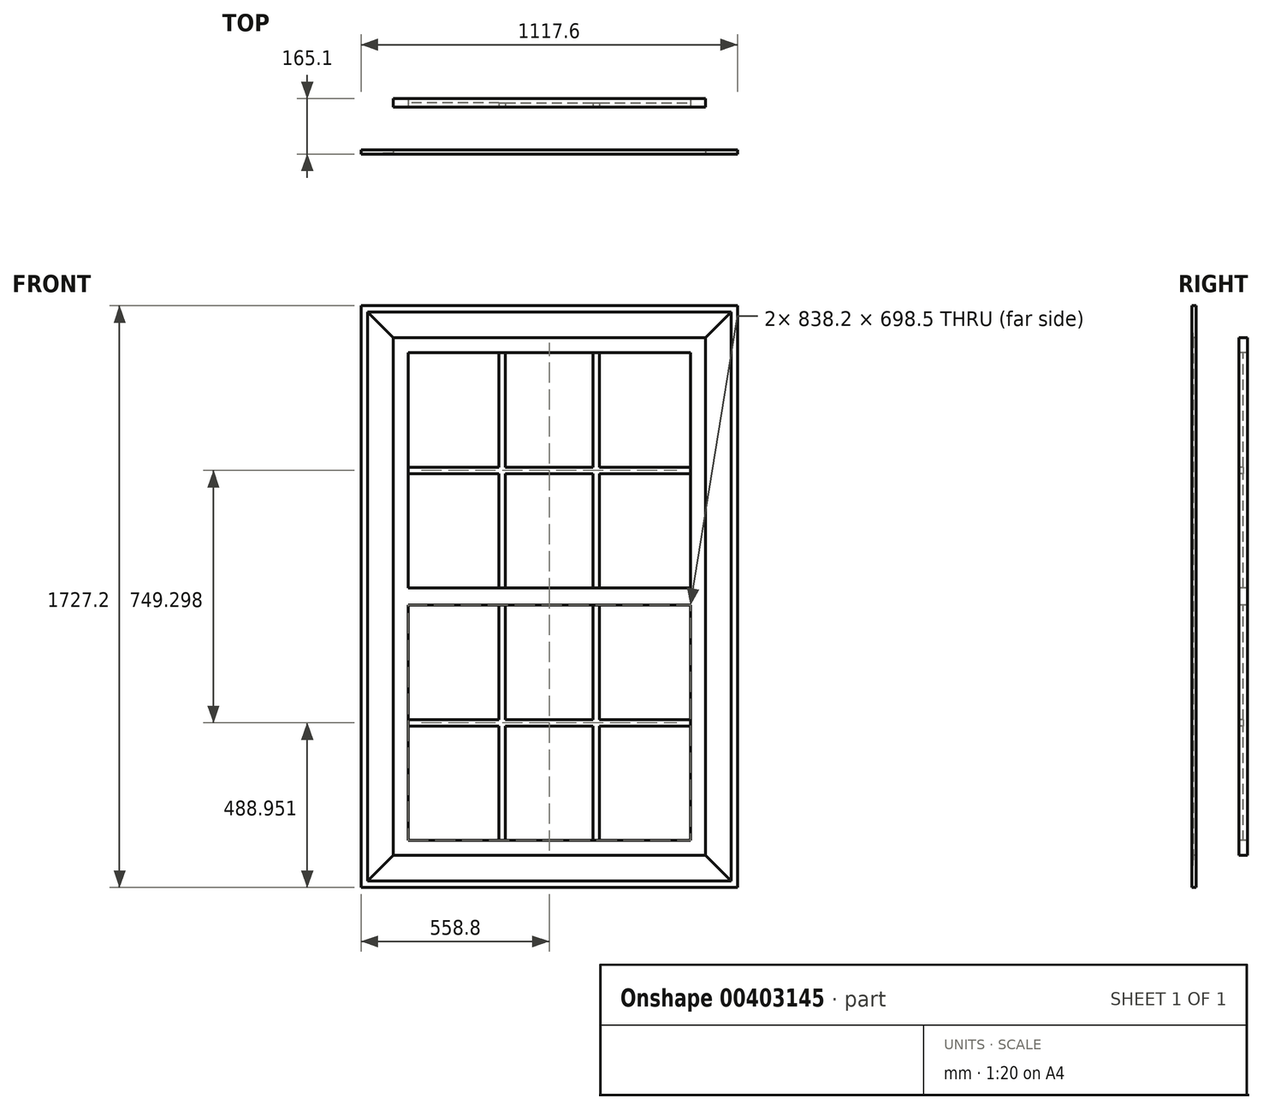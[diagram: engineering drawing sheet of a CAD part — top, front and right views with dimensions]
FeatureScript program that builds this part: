
annotation { "Feature Type Name" : "Feature", "Feature Type Description" : "" }
export const myFeature = defineFeature(function(context is Context, id is Id, definition is map)
    precondition{}
    {
        {
            var Q0;
            Q0=qCreatedBy(makeId("Front.planeOp"),FACE);
            var sketch = newSketch(context, id + "F0", { "sketchPlane" : qUnion([Q0])});
            skLineSegment(sketch, "E0.bottom", {"start": v(463.55, 768.35) * mm, "end": v(-463.55, 768.35) * mm});
            skLineSegment(sketch, "E0.top", {"start": v(463.55, -768.35) * mm, "end": v(-463.55, -768.35) * mm});
            skLineSegment(sketch, "E0.left", {"start": v(463.55, 768.35) * mm, "end": v(463.55, -768.35) * mm});
            skLineSegment(sketch, "E0.right", {"start": v(-463.55, 768.35) * mm, "end": v(-463.55, -768.35) * mm});
            skPoint(sketch, "E0.middle", {"position": v(0, 0) * mm});
            skLineSegment(sketch, "E1.0", {"start": v(-558.8, 863.6) * mm, "end": v(-558.8, -863.6) * mm});
            skLineSegment(sketch, "E1.1", {"start": v(558.8, 863.6) * mm, "end": v(-558.8, 863.6) * mm});
            skLineSegment(sketch, "E1.2", {"start": v(558.8, 863.6) * mm, "end": v(558.8, -863.6) * mm});
            skLineSegment(sketch, "E1.3", {"start": v(558.8, -863.6) * mm, "end": v(-558.8, -863.6) * mm});
            skLineSegment(sketch, "E2.0", {"start": v(-419.1, 723.9) * mm, "end": v(-419.1, -723.9) * mm});
            skLineSegment(sketch, "E2.1", {"start": v(419.1, 723.9) * mm, "end": v(-419.1, 723.9) * mm});
            skLineSegment(sketch, "E2.2", {"start": v(419.1, 723.9) * mm, "end": v(419.1, -723.9) * mm});
            skLineSegment(sketch, "E2.3", {"start": v(419.1, -723.9) * mm, "end": v(-419.1, -723.9) * mm});
            skLineSegment(sketch, "E3", {"start": v(-419.1, 0) * mm, "end": v(419.1, 0) * mm, "construction": true});
            skLineSegment(sketch, "E4.0", {"start": v(-419.1, 25.4) * mm, "end": v(419.1, 25.4) * mm});
            skLineSegment(sketch, "E5", {"start": v(-139.7, 723.9) * mm, "end": v(-139.7, 25.4) * mm, "construction": true});
            skLineSegment(sketch, "E6", {"start": v(139.7, 723.9) * mm, "end": v(139.7, 25.4) * mm, "construction": true});
            skLineSegment(sketch, "E7", {"start": v(-419.1, 374.65) * mm, "end": v(-139.7, 374.65) * mm, "construction": true});
            skLineSegment(sketch, "E8", {"start": v(-139.7, 374.65) * mm, "end": v(139.7, 374.65) * mm, "construction": true});
            skLineSegment(sketch, "E9", {"start": v(139.7, 374.65) * mm, "end": v(419.1, 374.65) * mm, "construction": true});
            skLineSegment(sketch, "E10", {"start": v(-419.1, 365.12) * mm, "end": v(-149.22, 365.12) * mm});
            skLineSegment(sketch, "E11", {"start": v(-149.22, 365.12) * mm, "end": v(-149.22, 25.4) * mm});
            skLineSegment(sketch, "E12", {"start": v(-419.1, 384.17) * mm, "end": v(-149.22, 384.17) * mm});
            skLineSegment(sketch, "E13", {"start": v(-149.22, 384.17) * mm, "end": v(-149.22, 723.9) * mm});
            skLineSegment(sketch, "E14", {"start": v(-130.17, 723.9) * mm, "end": v(-130.17, 384.17) * mm});
            skLineSegment(sketch, "E15", {"start": v(-130.17, 384.17) * mm, "end": v(130.17, 384.17) * mm});
            skLineSegment(sketch, "E16", {"start": v(130.17, 384.17) * mm, "end": v(130.17, 723.9) * mm});
            skLineSegment(sketch, "E17", {"start": v(149.22, 723.9) * mm, "end": v(149.22, 384.17) * mm});
            skLineSegment(sketch, "E18", {"start": v(149.22, 384.17) * mm, "end": v(419.1, 384.17) * mm});
            skLineSegment(sketch, "E19", {"start": v(419.1, 365.12) * mm, "end": v(149.22, 365.12) * mm});
            skLineSegment(sketch, "E20", {"start": v(149.22, 365.12) * mm, "end": v(149.22, 25.4) * mm});
            skLineSegment(sketch, "E21", {"start": v(130.17, 25.4) * mm, "end": v(130.17, 365.12) * mm});
            skLineSegment(sketch, "E22", {"start": v(130.17, 365.12) * mm, "end": v(-130.17, 365.12) * mm});
            skLineSegment(sketch, "E23", {"start": v(-130.17, 365.12) * mm, "end": v(-130.17, 25.4) * mm});
            skLineSegment(sketch, "E24", {"start": v(-149.22, 384.17) * mm, "end": v(-130.17, 365.12) * mm, "construction": true});
            skLineSegment(sketch, "E25", {"start": v(130.17, 384.17) * mm, "end": v(149.22, 365.12) * mm, "construction": true});
            skLineSegment(sketch, "E26.MirrorCS", {"start": v(-149.22, -384.17) * mm, "end": v(-130.17, -365.12) * mm, "construction": true});
            skLineSegment(sketch, "E27.MirrorCS", {"start": v(130.17, -384.17) * mm, "end": v(149.22, -365.12) * mm, "construction": true});
            skLineSegment(sketch, "E28.MirrorCS", {"start": v(-149.22, -365.12) * mm, "end": v(-149.22, -25.4) * mm});
            skLineSegment(sketch, "E29.MirrorCS", {"start": v(-130.17, -365.12) * mm, "end": v(-130.17, -25.4) * mm});
            skLineSegment(sketch, "E30.MirrorCS", {"start": v(-419.1, -365.12) * mm, "end": v(-149.22, -365.12) * mm});
            skLineSegment(sketch, "E31.MirrorCS", {"start": v(-419.1, -384.17) * mm, "end": v(-149.22, -384.17) * mm});
            skLineSegment(sketch, "E32.MirrorCS", {"start": v(-149.22, -384.17) * mm, "end": v(-149.22, -723.9) * mm});
            skLineSegment(sketch, "E33.MirrorCS", {"start": v(-130.17, -723.9) * mm, "end": v(-130.17, -384.17) * mm});
            skLineSegment(sketch, "E34.MirrorCS", {"start": v(-130.17, -384.17) * mm, "end": v(130.17, -384.17) * mm});
            skLineSegment(sketch, "E35.MirrorCS", {"start": v(130.17, -365.12) * mm, "end": v(-130.17, -365.12) * mm});
            skLineSegment(sketch, "E36.MirrorCS", {"start": v(130.17, -25.4) * mm, "end": v(130.17, -365.12) * mm});
            skLineSegment(sketch, "E37.MirrorCS", {"start": v(130.17, -384.17) * mm, "end": v(130.17, -723.9) * mm});
            skLineSegment(sketch, "E38.MirrorCS", {"start": v(149.22, -723.9) * mm, "end": v(149.22, -384.17) * mm});
            skLineSegment(sketch, "E39.MirrorCS", {"start": v(149.22, -365.12) * mm, "end": v(149.22, -25.4) * mm});
            skLineSegment(sketch, "E40.MirrorCS", {"start": v(419.1, -365.12) * mm, "end": v(149.22, -365.12) * mm});
            skLineSegment(sketch, "E41.MirrorCS", {"start": v(149.22, -384.17) * mm, "end": v(419.1, -384.17) * mm});
            skLineSegment(sketch, "E42.MirrorCS", {"start": v(-419.1, -25.4) * mm, "end": v(419.1, -25.4) * mm});
            skSolve(sketch);
        }
        {
            var Q0;
            Q0=makeQuery(id+"F0.imprint","IMPRINT",FACE,{"disambiguationData":[TD([[makeQuery(id+"F0.imprint","IMPRINT",EDGE,{"derivedFrom":sQuery(id+"F0.wireOp",EDGE,"E0.bottom")}),1.0]])]});
            var Q1;
            Q1=sQuery(id+"F0.wireOp",EDGE,"E0.right");
            var Q2;
            Q2=sQuery(id+"F0.wireOp",EDGE,"E0.bottom");
            var Q3;
            Q3=sQuery(id+"F0.wireOp",EDGE,"E0.left");
            var Q4;
            Q4=sQuery(id+"F0.wireOp",EDGE,"E0.top");
            extrude(context, id + "F1", {"entities" : qUnion([Q0]), "bodyType" : ToolBodyType.SURFACE, "surfaceEntities" : qUnion([Q1, Q2, Q3, Q4]), "oppositeDirection" : true, "depth" : 127 * mm});
        }
        {
            var Q0;
            Q0=makeQuery(id+"F1.opExtrude","CAP_VERTEX",VERTEX,{"disambiguationData":[OSD([sQuery(id+"F0.wireOp",VERTEX,"E0.left.start")])],"isStart":false});
            var Q1;
            Q1=makeQuery(id+"F1.opExtrude","CAP_VERTEX",VERTEX,{"disambiguationData":[OSD([sQuery(id+"F0.wireOp",VERTEX,"E0.bottom.end")])],"isStart":false});
            var Q2;
            Q2=makeQuery(id+"F1.opExtrude","CAP_VERTEX",VERTEX,{"disambiguationData":[OSD([sQuery(id+"F0.wireOp",VERTEX,"E0.top.end")])],"isStart":false});
            cPlane(context, id + "F2", {"entities" : qUnion([Q0, Q1, Q2]), "cplaneType" : CPlaneType.THREE_POINT, "offset" : 0 * mm, "width" : 152.4 * mm, "height" : 152.4 * mm});
        }
        {
            var Q0;
            Q0=qCreatedBy(id+"F2.planeOp",FACE);
            var sketch = newSketch(context, id + "F3", { "sketchPlane" : qUnion([Q0])});
            skLineSegment(sketch, "E43.0", {"start": v(-419.1, 723.9) * mm, "end": v(419.1, 723.9) * mm});
            skLineSegment(sketch, "E43.1", {"start": v(-419.1, 723.9) * mm, "end": v(-419.1, -723.9) * mm});
            skLineSegment(sketch, "E43.2", {"start": v(-419.1, -723.9) * mm, "end": v(419.1, -723.9) * mm});
            skLineSegment(sketch, "E43.3", {"start": v(419.1, 723.9) * mm, "end": v(419.1, -723.9) * mm});
            skLineSegment(sketch, "E43.4", {"start": v(463.55, 768.35) * mm, "end": v(463.55, -768.35) * mm});
            skLineSegment(sketch, "E43.5", {"start": v(-463.55, -768.35) * mm, "end": v(463.55, -768.35) * mm});
            skLineSegment(sketch, "E43.6", {"start": v(-463.55, 768.35) * mm, "end": v(-463.55, -768.35) * mm});
            skLineSegment(sketch, "E43.7", {"start": v(-463.55, 768.35) * mm, "end": v(463.55, 768.35) * mm});
            skLineSegment(sketch, "E44.0", {"start": v(419.1, -25.4) * mm, "end": v(-419.1, -25.4) * mm});
            skLineSegment(sketch, "E44.1", {"start": v(419.1, 25.4) * mm, "end": v(-419.1, 25.4) * mm});
            skSolve(sketch);
        }
        {
            var Q0;
            Q0=makeQuery(id+"F3.imprint","IMPRINT",FACE,{"disambiguationData":[TD([[makeQuery(id+"F3.imprint","IMPRINT",EDGE,{"derivedFrom":sQuery(id+"F3.wireOp",EDGE,"E43.0")}),1.0]])]});
            var Q1;
            {var subQ0=sQuery(id+"F3.wireOp",EDGE,"E44.0");Q1=makeQuery(id+"F3.imprint","IMPRINT",FACE,{"disambiguationData":[TD([[makeQuery(id+"F3.imprint","IMPRINT",EDGE,{"derivedFrom":subQ0}),-1.0]])]});}
            extrude(context, id + "F4", {"entities" : qUnion([Q0, Q1]), "depth" : 25.4 * mm});
        }
        {
            var Q0;
            Q0=makeQuery(id+"F4.opExtrude","CAP_FACE",FACE,{"disambiguationData":[OSD([sQuery(id+"F3.wireOp",EDGE,"E43.0"),sQuery(id+"F3.wireOp",EDGE,"E43.1"),sQuery(id+"F3.wireOp",EDGE,"E43.2"),sQuery(id+"F3.wireOp",EDGE,"E43.3"),sQuery(id+"F3.wireOp",EDGE,"E43.4"),sQuery(id+"F3.wireOp",EDGE,"E43.5"),sQuery(id+"F3.wireOp",EDGE,"E43.6"),sQuery(id+"F3.wireOp",EDGE,"E43.7")])],"isStart":true});
            var sketch = newSketch(context, id + "F5", { "sketchPlane" : qUnion([Q0])});
            skLineSegment(sketch, "E45.0.0", {"start": v(149.22, -723.9) * mm, "end": v(149.22, -384.17) * mm});
            skLineSegment(sketch, "E45.0.1", {"start": v(149.22, -384.17) * mm, "end": v(419.1, -384.17) * mm});
            skLineSegment(sketch, "E45.0.2", {"start": v(419.1, -384.17) * mm, "end": v(419.1, -365.12) * mm});
            skLineSegment(sketch, "E45.0.3", {"start": v(419.1, -365.12) * mm, "end": v(149.22, -365.12) * mm});
            skLineSegment(sketch, "E45.0.4", {"start": v(149.22, -365.12) * mm, "end": v(149.22, -25.4) * mm});
            skLineSegment(sketch, "E45.0.5", {"start": v(149.22, -25.4) * mm, "end": v(130.17, -25.4) * mm});
            skLineSegment(sketch, "E45.0.6", {"start": v(130.17, -25.4) * mm, "end": v(130.17, -365.12) * mm});
            skLineSegment(sketch, "E45.0.7", {"start": v(130.17, -365.12) * mm, "end": v(-130.17, -365.12) * mm});
            skLineSegment(sketch, "E45.0.8", {"start": v(-130.17, -365.12) * mm, "end": v(-130.17, -25.4) * mm});
            skLineSegment(sketch, "E45.0.9", {"start": v(-130.17, -25.4) * mm, "end": v(-149.22, -25.4) * mm});
            skLineSegment(sketch, "E45.0.10", {"start": v(-149.22, -25.4) * mm, "end": v(-149.22, -365.12) * mm});
            skLineSegment(sketch, "E45.0.11", {"start": v(-149.22, -365.12) * mm, "end": v(-419.1, -365.12) * mm});
            skLineSegment(sketch, "E45.0.12", {"start": v(-419.1, -365.12) * mm, "end": v(-419.1, -384.17) * mm});
            skLineSegment(sketch, "E45.0.13", {"start": v(-419.1, -384.17) * mm, "end": v(-149.22, -384.17) * mm});
            skLineSegment(sketch, "E45.0.14", {"start": v(-149.22, -384.17) * mm, "end": v(-149.22, -723.9) * mm});
            skLineSegment(sketch, "E45.0.15", {"start": v(-149.22, -723.9) * mm, "end": v(-130.17, -723.9) * mm});
            skLineSegment(sketch, "E45.0.16", {"start": v(-130.17, -723.9) * mm, "end": v(-130.17, -384.17) * mm});
            skLineSegment(sketch, "E45.0.17", {"start": v(-130.17, -384.17) * mm, "end": v(130.17, -384.17) * mm});
            skLineSegment(sketch, "E45.0.18", {"start": v(130.17, -384.17) * mm, "end": v(130.17, -723.9) * mm});
            skLineSegment(sketch, "E45.0.19", {"start": v(130.17, -723.9) * mm, "end": v(149.22, -723.9) * mm});
            skLineSegment(sketch, "E46.0.0", {"start": v(-130.17, 25.4) * mm, "end": v(-130.17, 365.12) * mm});
            skLineSegment(sketch, "E46.0.1", {"start": v(-130.17, 365.12) * mm, "end": v(130.17, 365.12) * mm});
            skLineSegment(sketch, "E46.0.2", {"start": v(130.17, 365.12) * mm, "end": v(130.17, 25.4) * mm});
            skLineSegment(sketch, "E46.0.3", {"start": v(130.17, 25.4) * mm, "end": v(149.22, 25.4) * mm});
            skLineSegment(sketch, "E46.0.4", {"start": v(149.22, 25.4) * mm, "end": v(149.22, 365.12) * mm});
            skLineSegment(sketch, "E46.0.5", {"start": v(149.22, 365.12) * mm, "end": v(419.1, 365.12) * mm});
            skLineSegment(sketch, "E46.0.6", {"start": v(419.1, 365.12) * mm, "end": v(419.1, 384.17) * mm});
            skLineSegment(sketch, "E46.0.7", {"start": v(419.1, 384.17) * mm, "end": v(149.22, 384.17) * mm});
            skLineSegment(sketch, "E46.0.8", {"start": v(149.22, 384.17) * mm, "end": v(149.22, 723.9) * mm});
            skLineSegment(sketch, "E46.0.9", {"start": v(149.22, 723.9) * mm, "end": v(130.17, 723.9) * mm});
            skLineSegment(sketch, "E46.0.10", {"start": v(130.17, 723.9) * mm, "end": v(130.17, 384.17) * mm});
            skLineSegment(sketch, "E46.0.11", {"start": v(130.17, 384.17) * mm, "end": v(-130.17, 384.17) * mm});
            skLineSegment(sketch, "E46.0.12", {"start": v(-130.17, 384.17) * mm, "end": v(-130.17, 723.9) * mm});
            skLineSegment(sketch, "E46.0.13", {"start": v(-130.17, 723.9) * mm, "end": v(-149.22, 723.9) * mm});
            skLineSegment(sketch, "E46.0.14", {"start": v(-149.22, 723.9) * mm, "end": v(-149.22, 384.17) * mm});
            skLineSegment(sketch, "E46.0.15", {"start": v(-149.22, 384.17) * mm, "end": v(-419.1, 384.17) * mm});
            skLineSegment(sketch, "E46.0.16", {"start": v(-419.1, 384.17) * mm, "end": v(-419.1, 365.12) * mm});
            skLineSegment(sketch, "E46.0.17", {"start": v(-419.1, 365.12) * mm, "end": v(-149.22, 365.12) * mm});
            skLineSegment(sketch, "E46.0.18", {"start": v(-149.22, 365.12) * mm, "end": v(-149.22, 25.4) * mm});
            skLineSegment(sketch, "E46.0.19", {"start": v(-149.22, 25.4) * mm, "end": v(-130.17, 25.4) * mm});
            skSolve(sketch);
        }
        {
            var Q0;
            Q0=makeQuery(id+"F5.imprint","IMPRINT",FACE,{"disambiguationData":[TD([[makeQuery(id+"F5.imprint","IMPRINT",EDGE,{"derivedFrom":sQuery(id+"F5.wireOp",EDGE,"E45.0.0")}),1.0]])]});
            var Q1;
            Q1=makeQuery(id+"F5.imprint","IMPRINT",FACE,{"disambiguationData":[TD([[makeQuery(id+"F5.imprint","IMPRINT",EDGE,{"derivedFrom":sQuery(id+"F5.wireOp",EDGE,"E46.0.0")}),1.0]])]});
            extrude(context, id + "F6", {"entities" : qUnion([Q0, Q1]), "oppositeDirection" : true, "depth" : 12.7 * mm});
        }
        {
            var Q0;
            Q0=qCreatedBy(makeId("Top.planeOp"),FACE);
            var sketch = newSketch(context, id + "F7", { "sketchPlane" : qUnion([Q0])});
            skLineSegment(sketch, "E47", {"start": v(-463.55, 0) * mm, "end": v(-463.55, -9.53) * mm});
            skLineSegment(sketch, "E48", {"start": v(-463.55, -9.53) * mm, "end": v(-539.75, -12.7) * mm});
            skLineSegment(sketch, "E49", {"start": v(-539.75, -12.7) * mm, "end": v(-558.8, -12.7) * mm});
            skLineSegment(sketch, "E50", {"start": v(-558.8, -12.7) * mm, "end": v(-558.8, 0) * mm});
            skLineSegment(sketch, "E51", {"start": v(-558.8, 0) * mm, "end": v(-463.55, 0) * mm});
            skSolve(sketch);
        }
        {
            var Q0;
            Q0=makeQuery(id+"F7.imprint","IMPRINT",FACE,{"disambiguationData":[TD([[makeQuery(id+"F7.imprint","IMPRINT",EDGE,{"derivedFrom":sQuery(id+"F7.wireOp",EDGE,"E47")}),-1.0]])]});
            var Q1;
            Q1=sQuery(id+"F0.wireOp",EDGE,"E1.0");
            var Q2;
            Q2=sQuery(id+"F0.wireOp",EDGE,"E1.1");
            var Q3;
            Q3=sQuery(id+"F0.wireOp",EDGE,"E1.2");
            var Q4;
            Q4=sQuery(id+"F0.wireOp",EDGE,"E1.3");
            sweep(context, id + "F8", {"profiles" : qUnion([Q0]), "path" : qUnion([Q1, Q2, Q3, Q4])});
        }
    });
